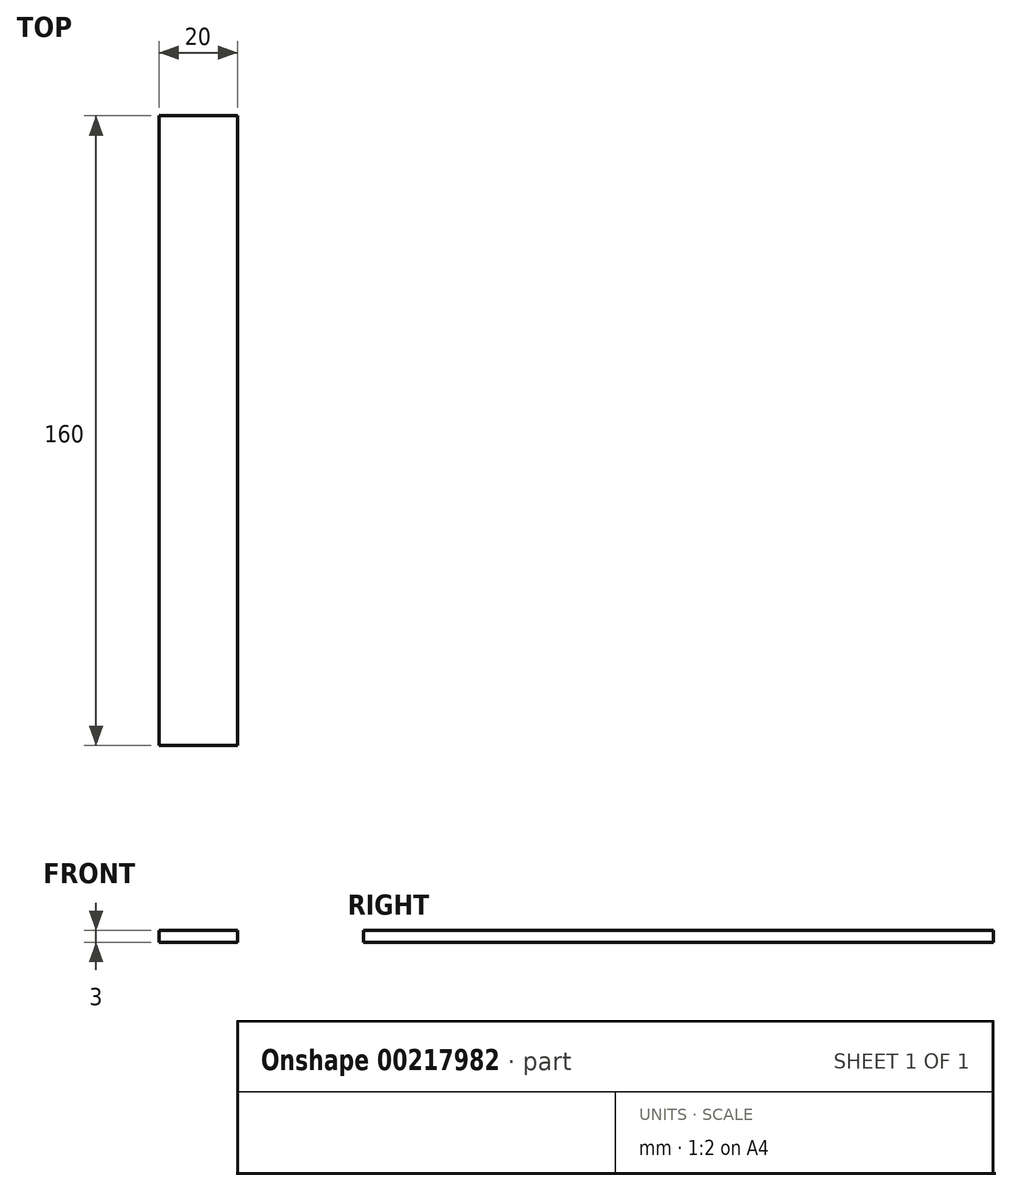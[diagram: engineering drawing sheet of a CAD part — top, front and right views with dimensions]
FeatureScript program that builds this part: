
annotation { "Feature Type Name" : "Feature", "Feature Type Description" : "" }
export const myFeature = defineFeature(function(context is Context, id is Id, definition is map)
    precondition{}
    {
        {
            var Q0;
            Q0=qCreatedBy(makeId("Top.planeOp"),FACE);
            var sketch = newSketch(context, id + "F0", { "sketchPlane" : qUnion([Q0])});
            skLineSegment(sketch, "E0.bottom", {"start": v(-7.5, 133.81) * mm, "end": v(12.5, 133.81) * mm});
            skLineSegment(sketch, "E0.top", {"start": v(-7.5, -26.19) * mm, "end": v(12.5, -26.19) * mm});
            skLineSegment(sketch, "E0.left", {"start": v(-7.5, 133.81) * mm, "end": v(-7.5, -26.19) * mm});
            skLineSegment(sketch, "E0.right", {"start": v(12.5, 133.81) * mm, "end": v(12.5, -26.19) * mm});
            skSolve(sketch);
        }
        {
            var Q0;
            Q0 = qSketchRegion(id + "F0", true);
            extrude(context, id + "F1", {"entities" : qUnion([Q0]), "depth" : 3 * mm});
        }
    });
